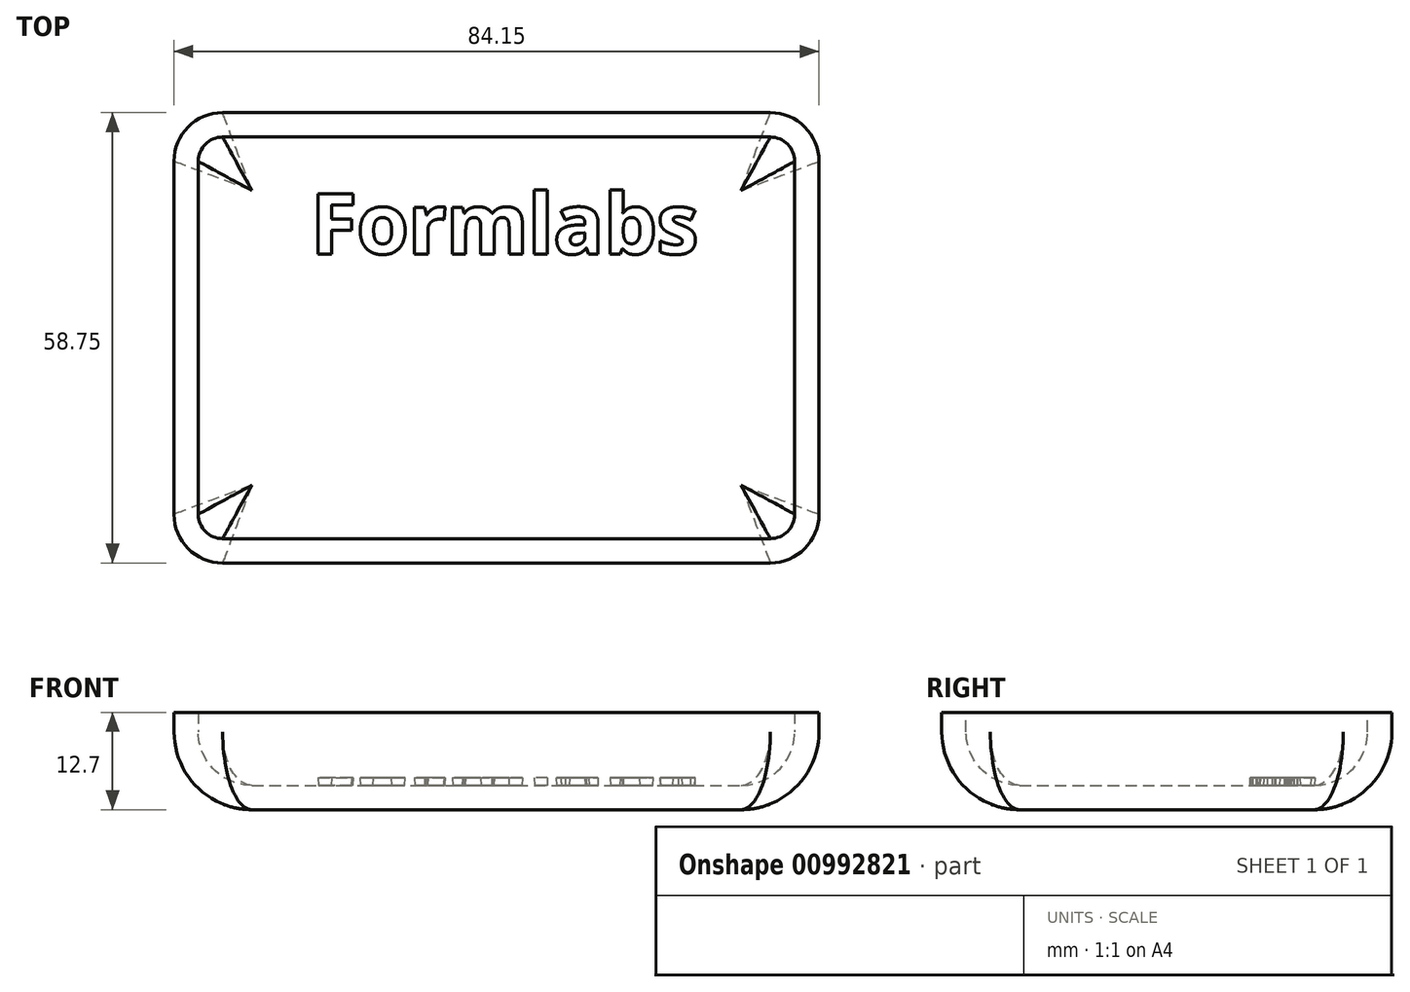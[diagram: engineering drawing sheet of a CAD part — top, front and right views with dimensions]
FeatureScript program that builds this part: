
annotation { "Feature Type Name" : "Feature", "Feature Type Description" : "" }
export const myFeature = defineFeature(function(context is Context, id is Id, definition is map)
    precondition{}
    {
        {
            var Q0;
            Q0=qCreatedBy(makeId("Top.planeOp"),FACE);
            var sketch = newSketch(context, id + "F0", { "sketchPlane" : qUnion([Q0])});
            skLineSegment(sketch, "E0.bottom", {"start": v(-55.65, 0) * mm, "end": v(15.8, 0) * mm});
            skLineSegment(sketch, "E0.top", {"start": v(-55.65, -58.75) * mm, "end": v(15.8, -58.75) * mm});
            skLineSegment(sketch, "E0.left", {"start": v(-62, -6.35) * mm, "end": v(-62, -52.4) * mm});
            skLineSegment(sketch, "E0.right", {"start": v(22.15, -6.35) * mm, "end": v(22.15, -52.4) * mm});
            skPoint(sketch, "E1.visualSharp", {"position": v(-62, -58.75) * mm});
            skArc(sketch, "E1.filletArc", {"start": v(-62, -52.4) * mm, "mid": v(-60.14, -56.9) * mm, "end": v(-55.65, -58.75) * mm});
            skPoint(sketch, "E2.visualSharp", {"position": v(-62, 0) * mm});
            skArc(sketch, "E2.filletArc", {"start": v(-55.65, 0) * mm, "mid": v(-60.14, -1.86) * mm, "end": v(-62, -6.35) * mm});
            skPoint(sketch, "E3.visualSharp", {"position": v(22.15, 0) * mm});
            skArc(sketch, "E3.filletArc", {"start": v(22.15, -6.35) * mm, "mid": v(20.29, -1.86) * mm, "end": v(15.8, 0) * mm});
            skPoint(sketch, "E4.visualSharp", {"position": v(22.15, -58.75) * mm});
            skArc(sketch, "E4.filletArc", {"start": v(15.8, -58.75) * mm, "mid": v(20.29, -56.9) * mm, "end": v(22.15, -52.4) * mm});
            skSolve(sketch);
        }
        {
            var Q0;
            Q0=makeQuery(id+"F0.imprint","IMPRINT",FACE,{"disambiguationData":[TD([[makeQuery(id+"F0.imprint","IMPRINT",EDGE,{"derivedFrom":sQuery(id+"F0.wireOp",EDGE,"E0.bottom")}),-1.0]])]});
            extrude(context, id + "F1", {"entities" : qUnion([Q0]), "depth" : 12.7 * mm, "offsetDistance" : 25.4 * mm});
        }
        {
            var Q0;
            Q0=makeQuery(id+"F1.opExtrude","CAP_EDGE",EDGE,{"disambiguationData":[OSD([sQuery(id+"F0.wireOp",EDGE,"E0.top")])],"isStart":true});
            var Q1;
            Q1=makeQuery(id+"F1.opExtrude","CAP_EDGE",EDGE,{"disambiguationData":[OSD([sQuery(id+"F0.wireOp",EDGE,"E4.filletArc")])],"isStart":true});
            var Q2;
            Q2=makeQuery(id+"F1.opExtrude","CAP_EDGE",EDGE,{"disambiguationData":[OSD([sQuery(id+"F0.wireOp",EDGE,"E0.right")])],"isStart":true});
            var Q3;
            Q3=makeQuery(id+"F1.opExtrude","CAP_EDGE",EDGE,{"disambiguationData":[OSD([sQuery(id+"F0.wireOp",EDGE,"E3.filletArc")])],"isStart":true});
            var Q4;
            Q4=makeQuery(id+"F1.opExtrude","CAP_EDGE",EDGE,{"disambiguationData":[OSD([sQuery(id+"F0.wireOp",EDGE,"E0.bottom")])],"isStart":true});
            var Q5;
            Q5=makeQuery(id+"F1.opExtrude","CAP_EDGE",EDGE,{"disambiguationData":[OSD([sQuery(id+"F0.wireOp",EDGE,"E2.filletArc")])],"isStart":true});
            var Q6;
            Q6=makeQuery(id+"F1.opExtrude","CAP_EDGE",EDGE,{"disambiguationData":[OSD([sQuery(id+"F0.wireOp",EDGE,"E0.left")])],"isStart":true});
            fillet(context, id + "F2", {"entities" : qUnion([Q0, Q1, Q2, Q3, Q4, Q5, Q6]), "radius" : 10.16 * mm, "tangentPropagation" : true, "allowEdgeOverflow" : false});
        }
        {
            var Q0;
            Q0=makeQuery(id+"F1.opExtrude","CAP_FACE",FACE,{"disambiguationData":[OSD([sQuery(id+"F0.wireOp",EDGE,"E0.bottom"),sQuery(id+"F0.wireOp",EDGE,"E0.top"),sQuery(id+"F0.wireOp",EDGE,"E0.left"),sQuery(id+"F0.wireOp",EDGE,"E0.right"),sQuery(id+"F0.wireOp",EDGE,"E1.filletArc"),sQuery(id+"F0.wireOp",EDGE,"E2.filletArc"),sQuery(id+"F0.wireOp",EDGE,"E3.filletArc"),sQuery(id+"F0.wireOp",EDGE,"E4.filletArc")])],"isStart":false});
            shell(context, id + "F3", {"entities" : qUnion([Q0]), "thickness" : 3.17 * mm});
        }
        {
            var Q0;
            Q0=makeQuery(id+"F3.opShell","OFFSET_FACE",FACE,{"disambiguationData":[OSD([sQuery(id+"F0.wireOp",EDGE,"E0.bottom"),sQuery(id+"F0.wireOp",EDGE,"E0.top"),sQuery(id+"F0.wireOp",EDGE,"E0.left"),sQuery(id+"F0.wireOp",EDGE,"E0.right"),sQuery(id+"F0.wireOp",EDGE,"E1.filletArc"),sQuery(id+"F0.wireOp",EDGE,"E2.filletArc"),sQuery(id+"F0.wireOp",EDGE,"E3.filletArc"),sQuery(id+"F0.wireOp",EDGE,"E4.filletArc")])]});
            var sketch = newSketch(context, id + "F4", { "sketchPlane" : qUnion([Q0])});
            skText(sketch, "E5", { "text": "Formlabs", "fontName": "OpenSans-Bold.ttf"});
            const initialGuessF4  = {"E5": [-0.04411, -0.01837, 1, 0, 0.00783]};
            skSetInitialGuess(sketch, initialGuessF4);
            skSolve(sketch);
        }
        {
            var Q0;
            Q0 = qSketchRegion(id + "F4", true);
            extrude(context, id + "F5", {"entities" : qUnion([Q0]), "depth" : 1.02 * mm, "offsetDistance" : 25.4 * mm, "hasDraft" : true, "draftAngle" : 3 * degree});
        }
    });
